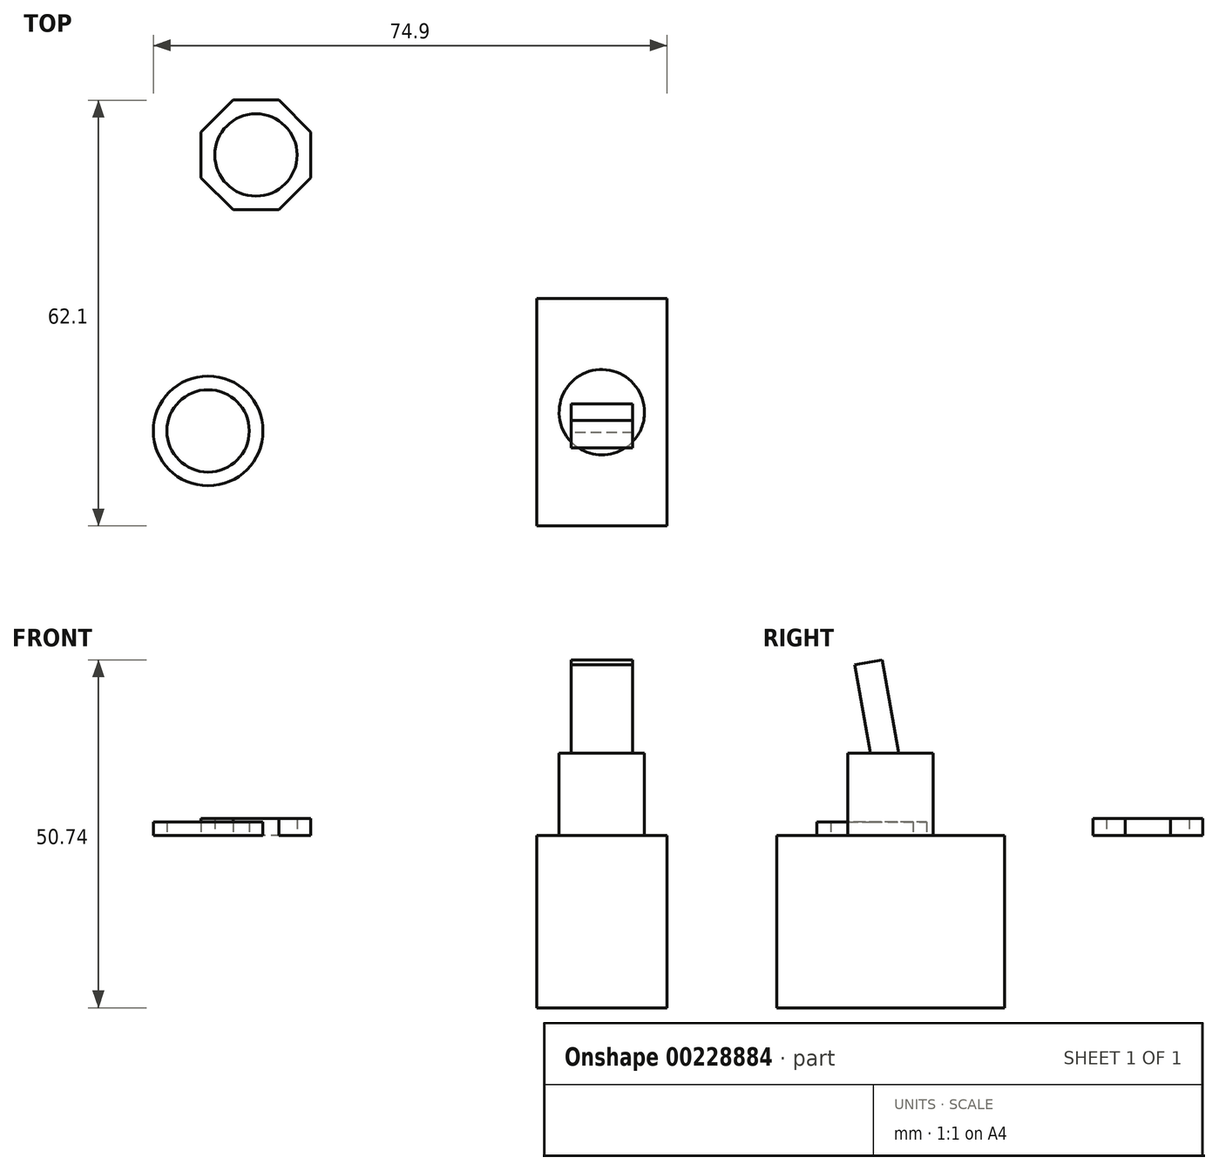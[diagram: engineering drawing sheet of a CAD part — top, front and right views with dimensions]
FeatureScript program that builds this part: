
annotation { "Feature Type Name" : "Feature", "Feature Type Description" : "" }
export const myFeature = defineFeature(function(context is Context, id is Id, definition is map)
    precondition{}
    {
        {
            var Q0;
            Q0=qCreatedBy(makeId("Top.planeOp"),FACE);
            var sketch = newSketch(context, id + "F0", { "sketchPlane" : qUnion([Q0])});
            skLineSegment(sketch, "E0.bottom", {"start": v(9.5, 16.6) * mm, "end": v(-9.5, 16.6) * mm});
            skLineSegment(sketch, "E0.top", {"start": v(9.5, -16.6) * mm, "end": v(-9.5, -16.6) * mm});
            skLineSegment(sketch, "E0.left", {"start": v(9.5, 16.6) * mm, "end": v(9.5, -16.6) * mm});
            skLineSegment(sketch, "E0.right", {"start": v(-9.5, 16.6) * mm, "end": v(-9.5, -16.6) * mm});
            skPoint(sketch, "E0.middle", {"position": v(0, 0) * mm});
            skSolve(sketch);
        }
        {
            var Q0;
            Q0 = qSketchRegion(id + "F0", true);
            extrude(context, id + "F1", {"entities" : qUnion([Q0]), "oppositeDirection" : true, "depth" : 25.1 * mm});
        }
        {
            var Q0;
            Q0=qCreatedBy(makeId("Top.planeOp"),FACE);
            var sketch = newSketch(context, id + "F2", { "sketchPlane" : qUnion([Q0])});
            skCircle(sketch, "E1", {"center": v(0, 0) * mm, "radius": 6.22 * mm});
            skSolve(sketch);
        }
        {
            var Q0;
            Q0=makeQuery(id+"F2.imprint","IMPRINT",FACE,{"disambiguationData":[TD([[makeQuery(id+"F2.imprint","IMPRINT",EDGE,{"derivedFrom":sQuery(id+"F2.wireOp",EDGE,"E1")}),1.0]])]});
            var Q1;
            Q1=sQuery(id+"F2.wireOp",EDGE,"E1");
            extrude(context, id + "F3", {"entities" : qUnion([Q0]), "operationType" : NewBodyOperationType.ADD, "surfaceEntities" : qUnion([Q1]), "depth" : 12 * mm});
        }
        {
            var Q0;
            Q0=qCreatedBy(makeId("Top.planeOp"),FACE);
            cPlane(context, id + "F4", {"entities" : qUnion([Q0]), "cplaneType" : CPlaneType.OFFSET, "offset" : 7 * mm, "width" : 150 * mm, "height" : 150 * mm});
        }
        {
            var Q0;
            Q0=qCreatedBy(id+"F4.planeOp",FACE);
            var sketch = newSketch(context, id + "F5", { "sketchPlane" : qUnion([Q0])});
            skLineSegment(sketch, "E2", {"start": v(-5.88, 0) * mm, "end": v(6.17, 0) * mm, "construction": true});
            skSolve(sketch);
        }
        {
            var Q0;
            Q0=qCreatedBy(makeId("Front.planeOp"),FACE);
            var Q1;
            Q1=sQuery(id+"F5.wireOp",EDGE,"E2");
            cPlane(context, id + "F6", {"entities" : qUnion([Q0, Q1]), "cplaneType" : CPlaneType.LINE_ANGLE, "offset" : 25 * mm, "angle" : 10 * degree, "width" : 150 * mm, "height" : 150 * mm});
        }
        {
            var Q0;
            Q0=qCreatedBy(id+"F6.planeOp",FACE);
            var sketch = newSketch(context, id + "F7", { "sketchPlane" : qUnion([Q0])});
            skLineSegment(sketch, "E3.bottom", {"start": v(-4.5, 5.5) * mm, "end": v(4.5, 5.5) * mm});
            skLineSegment(sketch, "E3.top", {"start": v(-4.5, 25.46) * mm, "end": v(4.5, 25.46) * mm});
            skLineSegment(sketch, "E3.left", {"start": v(-4.5, 5.5) * mm, "end": v(-4.5, 25.46) * mm});
            skLineSegment(sketch, "E3.right", {"start": v(4.5, 5.5) * mm, "end": v(4.5, 25.46) * mm});
            skSolve(sketch);
        }
        {
            var Q0;
            Q0 = qSketchRegion(id + "F7", true);
            extrude(context, id + "F8", {"entities" : qUnion([Q0]), "operationType" : NewBodyOperationType.ADD, "endBound" : BoundingType.SYMMETRIC, "depth" : 4.08 * mm});
        }
        {
            var Q0;
            Q0=qCreatedBy(makeId("Top.planeOp"),FACE);
            var sketch = newSketch(context, id + "F9", { "sketchPlane" : qUnion([Q0])});
            skCircle(sketch, "E4", {"center": v(-50.42, 37.5) * mm, "radius": 6 * mm});
            skCircle(sketch, "E5.cCircle", {"center": v(-50.42, 37.5) * mm, "radius": 8 * mm, "construction": true});
            skLineSegment(sketch, "E5.0", {"start": v(-53.74, 45.5) * mm, "end": v(-47.1, 45.5) * mm});
            skLineSegment(sketch, "E5.1", {"start": v(-47.1, 45.5) * mm, "end": v(-42.42, 40.82) * mm});
            skLineSegment(sketch, "E5.2", {"start": v(-42.42, 40.82) * mm, "end": v(-42.42, 34.19) * mm});
            skLineSegment(sketch, "E5.3", {"start": v(-42.42, 34.19) * mm, "end": v(-47.1, 29.5) * mm});
            skLineSegment(sketch, "E5.4", {"start": v(-47.1, 29.5) * mm, "end": v(-53.74, 29.5) * mm});
            skLineSegment(sketch, "E5.5", {"start": v(-53.74, 29.5) * mm, "end": v(-58.42, 34.19) * mm});
            skLineSegment(sketch, "E5.6", {"start": v(-58.42, 34.19) * mm, "end": v(-58.42, 40.82) * mm});
            skLineSegment(sketch, "E5.7", {"start": v(-58.42, 40.82) * mm, "end": v(-53.74, 45.5) * mm});
            skPoint(sketch, "E5.0.midPoint", {"position": v(-50.42, 45.5) * mm});
            skCircle(sketch, "E6", {"center": v(-57.4, -2.73) * mm, "radius": 6 * mm});
            skCircle(sketch, "E7", {"center": v(-57.4, -2.73) * mm, "radius": 8 * mm});
            skSolve(sketch);
        }
        {
            var Q0;
            Q0=makeQuery(id+"F9.imprint","IMPRINT",FACE,{"disambiguationData":[TD([[makeQuery(id+"F9.imprint","IMPRINT",EDGE,{"derivedFrom":sQuery(id+"F9.wireOp",EDGE,"E6")}),-1.0]])]});
            var Q1;
            Q1=sQuery(id+"F9.wireOp",EDGE,"E7");
            extrude(context, id + "F10", {"entities" : qUnion([Q0]), "surfaceEntities" : qUnion([Q1]), "depth" : 2 * mm});
        }
        {
            var Q0;
            Q0=makeQuery(id+"F9.imprint","IMPRINT",FACE,{"disambiguationData":[TD([[makeQuery(id+"F9.imprint","IMPRINT",EDGE,{"derivedFrom":sQuery(id+"F9.wireOp",EDGE,"E4")}),-1.0]])]});
            extrude(context, id + "F11", {"entities" : qUnion([Q0]), "depth" : 2.5 * mm});
        }
    });
